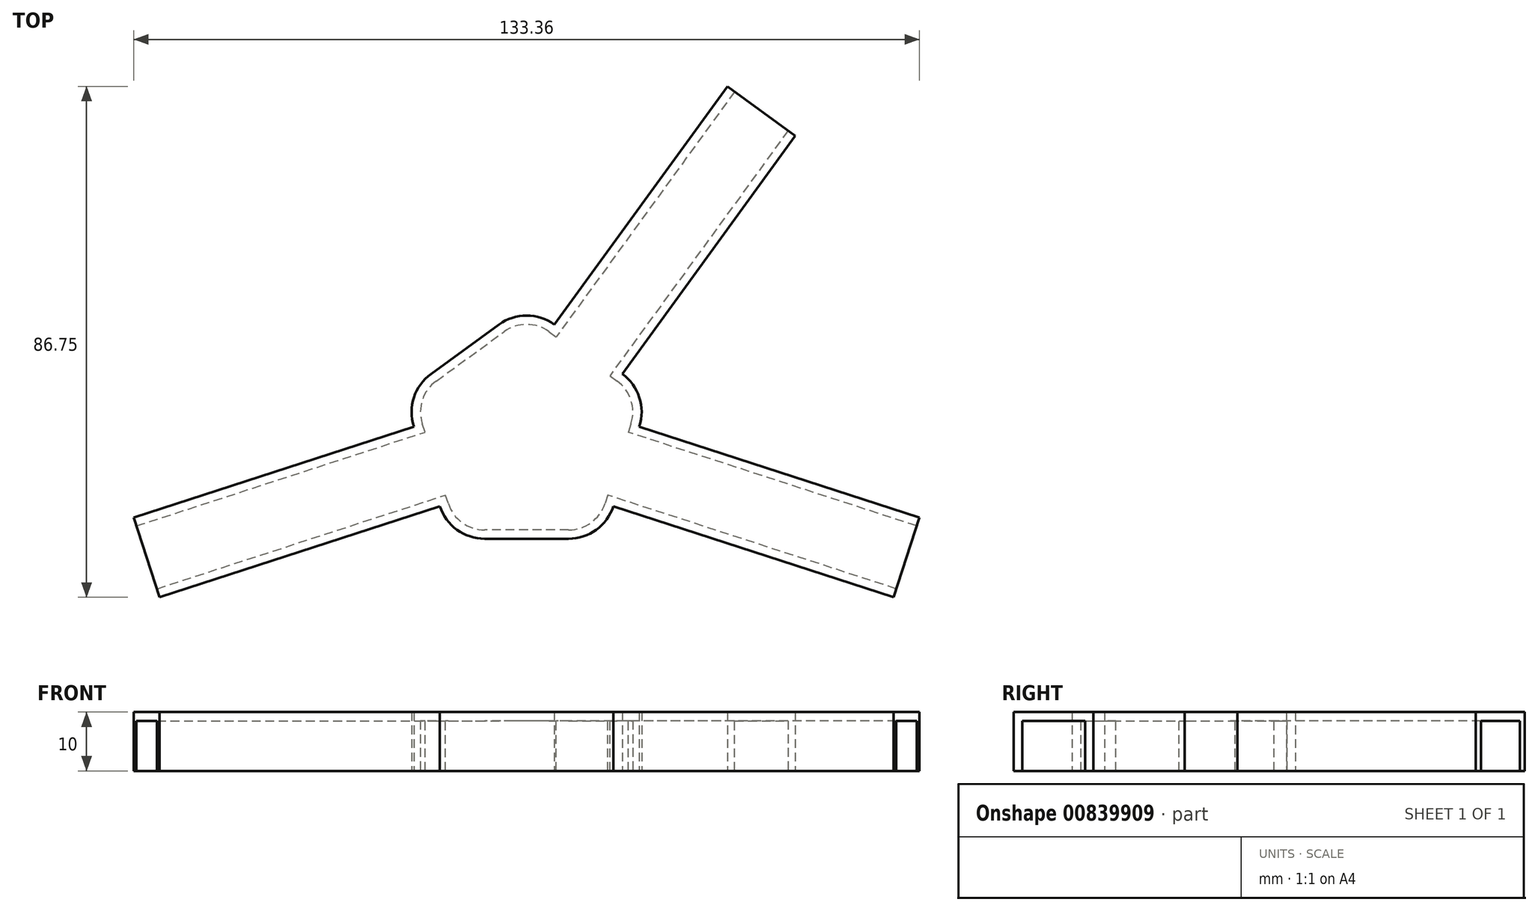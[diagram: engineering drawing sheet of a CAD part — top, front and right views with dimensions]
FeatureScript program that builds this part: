
annotation { "Feature Type Name" : "Feature", "Feature Type Description" : "" }
export const myFeature = defineFeature(function(context is Context, id is Id, definition is map)
    precondition{}
    {
        {
            var Q0;
            Q0=qCreatedBy(makeId("Top.planeOp"),FACE);
            var sketch = newSketch(context, id + "F0", { "sketchPlane" : qUnion([Q0])});
            skCircle(sketch, "E0.cCircle", {"center": v(0, 0) * mm, "radius": 22 * mm, "construction": true});
            skLineSegment(sketch, "E0.0", {"start": v(0, 22) * mm, "end": v(20.92, 6.8) * mm});
            skLineSegment(sketch, "E0.1", {"start": v(20.92, 6.8) * mm, "end": v(12.93, -17.8) * mm});
            skLineSegment(sketch, "E0.2", {"start": v(12.93, -17.8) * mm, "end": v(-12.93, -17.8) * mm});
            skLineSegment(sketch, "E0.3", {"start": v(-12.93, -17.8) * mm, "end": v(-20.92, 6.8) * mm});
            skLineSegment(sketch, "E0.4", {"start": v(-20.92, 6.8) * mm, "end": v(0, 22) * mm});
            skSolve(sketch);
        }
        {
            var Q0;
            Q0=makeQuery(id+"F0.imprint","IMPRINT",FACE,{"disambiguationData":[TD([[makeQuery(id+"F0.imprint","IMPRINT",EDGE,{"derivedFrom":sQuery(id+"F0.wireOp",EDGE,"E0.0")}),-1.0]])]});
            extrude(context, id + "F1", {"entities" : qUnion([Q0]), "depth" : 10 * mm, "offsetDistance" : 25 * mm});
        }
        {
            var Q0;
            Q0=makeQuery(id+"F1.opExtrude","SWEPT_EDGE",EDGE,{"disambiguationData":[OSD([sQuery(id+"F0.wireOp",EDGE,"E0.0"),sQuery(id+"F0.wireOp",EDGE,"E0.1")])]});
            var Q1;
            Q1=makeQuery(id+"F1.opExtrude","SWEPT_EDGE",EDGE,{"disambiguationData":[OSD([sQuery(id+"F0.wireOp",EDGE,"E0.0"),sQuery(id+"F0.wireOp",EDGE,"E0.4")])]});
            var Q2;
            Q2=makeQuery(id+"F1.opExtrude","SWEPT_EDGE",EDGE,{"disambiguationData":[OSD([sQuery(id+"F0.wireOp",EDGE,"E0.1"),sQuery(id+"F0.wireOp",EDGE,"E0.2")])]});
            var Q3;
            Q3=makeQuery(id+"F1.opExtrude","SWEPT_EDGE",EDGE,{"disambiguationData":[OSD([sQuery(id+"F0.wireOp",EDGE,"E0.2"),sQuery(id+"F0.wireOp",EDGE,"E0.3")])]});
            var Q4;
            Q4=makeQuery(id+"F1.opExtrude","SWEPT_EDGE",EDGE,{"disambiguationData":[OSD([sQuery(id+"F0.wireOp",EDGE,"E0.3"),sQuery(id+"F0.wireOp",EDGE,"E0.4")])]});
            fillet(context, id + "F2", {"entities" : qUnion([Q0, Q1, Q2, Q3, Q4]), "radius" : 8 * mm, "tangentPropagation" : true, "allowEdgeOverflow" : false});
        }
        {
            var Q0;
            Q0=makeQuery(id+"F1.opExtrude","CAP_FACE",FACE,{"disambiguationData":[OSD([sQuery(id+"F0.wireOp",EDGE,"E0.0"),sQuery(id+"F0.wireOp",EDGE,"E0.1"),sQuery(id+"F0.wireOp",EDGE,"E0.2"),sQuery(id+"F0.wireOp",EDGE,"E0.3"),sQuery(id+"F0.wireOp",EDGE,"E0.4")])],"isStart":true});
            shell(context, id + "F3", {"entities" : qUnion([Q0]), "thickness" : 1.5 * mm});
        }
        {
            var Q0;
            Q0=makeQuery(id+"F1.opExtrude","SWEPT_FACE",FACE,{"disambiguationData":[OSD([sQuery(id+"F0.wireOp",EDGE,"E0.1")])]});
            var sketch = newSketch(context, id + "F4", { "sketchPlane" : qUnion([Q0])});
            skLineSegment(sketch, "E1.bottom", {"start": v(-7.12, 10) * mm, "end": v(7.12, 10) * mm});
            skLineSegment(sketch, "E1.top", {"start": v(-7.12, 0) * mm, "end": v(7.12, 0) * mm});
            skLineSegment(sketch, "E1.left", {"start": v(-7.12, 10) * mm, "end": v(-7.12, 0) * mm});
            skLineSegment(sketch, "E1.right", {"start": v(7.12, 10) * mm, "end": v(7.12, 0) * mm});
            skPoint(sketch, "E1.middle", {"position": v(0, 5) * mm});
            skSolve(sketch);
        }
        {
            var Q0;
            Q0=makeQuery(id+"F4.imprint","IMPRINT",FACE,{"disambiguationData":[TD([[makeQuery(id+"F4.imprint","IMPRINT",EDGE,{"derivedFrom":sQuery(id+"F4.wireOp",EDGE,"E1.bottom")}),1.0]])]});
            extrude(context, id + "F5", {"entities" : qUnion([Q0]), "operationType" : NewBodyOperationType.ADD, "depth" : 50 * mm, "offsetDistance" : 25 * mm});
        }
        {
            var Q0;
            Q0=makeQuery(id+"F1.opExtrude","SWEPT_FACE",FACE,{"disambiguationData":[OSD([sQuery(id+"F0.wireOp",EDGE,"E0.3")])]});
            var sketch = newSketch(context, id + "F6", { "sketchPlane" : qUnion([Q0])});
            skLineSegment(sketch, "E2.bottom", {"start": v(-7.12, 10) * mm, "end": v(7.12, 10) * mm});
            skLineSegment(sketch, "E2.top", {"start": v(-7.12, 0) * mm, "end": v(7.12, 0) * mm});
            skLineSegment(sketch, "E2.left", {"start": v(-7.12, 10) * mm, "end": v(-7.12, 0) * mm});
            skLineSegment(sketch, "E2.right", {"start": v(7.12, 10) * mm, "end": v(7.12, 0) * mm});
            skPoint(sketch, "E2.middle", {"position": v(0, 5) * mm});
            skSolve(sketch);
        }
        {
            var Q0;
            Q0=makeQuery(id+"F1.opExtrude","SWEPT_FACE",FACE,{"disambiguationData":[OSD([sQuery(id+"F0.wireOp",EDGE,"E0.0")])]});
            var sketch = newSketch(context, id + "F7", { "sketchPlane" : qUnion([Q0])});
            skLineSegment(sketch, "E3.bottom", {"start": v(-7.12, 10) * mm, "end": v(7.12, 10) * mm});
            skLineSegment(sketch, "E3.top", {"start": v(-7.12, 0) * mm, "end": v(7.12, 0) * mm});
            skLineSegment(sketch, "E3.left", {"start": v(-7.12, 10) * mm, "end": v(-7.12, 0) * mm});
            skLineSegment(sketch, "E3.right", {"start": v(7.12, 10) * mm, "end": v(7.12, 0) * mm});
            skPoint(sketch, "E3.middle", {"position": v(0, 5) * mm});
            skSolve(sketch);
        }
        {
            var Q0;
            Q0=makeQuery(id+"F7.imprint","IMPRINT",FACE,{"disambiguationData":[TD([[makeQuery(id+"F7.imprint","IMPRINT",EDGE,{"derivedFrom":sQuery(id+"F7.wireOp",EDGE,"E3.bottom")}),1.0]])]});
            extrude(context, id + "F8", {"entities" : qUnion([Q0]), "operationType" : NewBodyOperationType.ADD, "depth" : 50 * mm, "offsetDistance" : 25 * mm});
        }
        {
            var Q0;
            Q0=makeQuery(id+"F6.imprint","IMPRINT",FACE,{"disambiguationData":[TD([[makeQuery(id+"F6.imprint","IMPRINT",EDGE,{"derivedFrom":sQuery(id+"F6.wireOp",EDGE,"E2.bottom")}),1.0]])]});
            extrude(context, id + "F9", {"entities" : qUnion([Q0]), "operationType" : NewBodyOperationType.ADD, "depth" : 50 * mm, "offsetDistance" : 25 * mm});
        }
        {
            var Q0;
            Q0=makeQuery(id+"F8.opExtrude","CAP_FACE",FACE,{"disambiguationData":[OSD([sQuery(id+"F7.wireOp",EDGE,"E3.bottom"),sQuery(id+"F7.wireOp",EDGE,"E3.top"),sQuery(id+"F7.wireOp",EDGE,"E3.left"),sQuery(id+"F7.wireOp",EDGE,"E3.right")])],"isStart":false});
            var Q1;
            Q1=makeQuery(id+"F3.opShell","OFFSET_FACE",FACE,{"disambiguationData":[OSD([sQuery(id+"F0.wireOp",EDGE,"E0.0")])]});
            var Q2;
            Q2=makeQuery(id+"F9.opExtrude","CAP_FACE",FACE,{"disambiguationData":[OSD([sQuery(id+"F6.wireOp",EDGE,"E2.bottom"),sQuery(id+"F6.wireOp",EDGE,"E2.top"),sQuery(id+"F6.wireOp",EDGE,"E2.left"),sQuery(id+"F6.wireOp",EDGE,"E2.right")])],"isStart":false});
            var Q3;
            Q3=makeQuery(id+"F3.opShell","OFFSET_FACE",FACE,{"disambiguationData":[OSD([sQuery(id+"F0.wireOp",EDGE,"E0.3")])]});
            var Q4;
            Q4=makeQuery(id+"F5.opExtrude","CAP_FACE",FACE,{"disambiguationData":[OSD([sQuery(id+"F4.wireOp",EDGE,"E1.bottom"),sQuery(id+"F4.wireOp",EDGE,"E1.top"),sQuery(id+"F4.wireOp",EDGE,"E1.left"),sQuery(id+"F4.wireOp",EDGE,"E1.right")])],"isStart":false});
            var Q5;
            Q5=makeQuery(id+"F3.opShell","OFFSET_FACE",FACE,{"disambiguationData":[OSD([sQuery(id+"F0.wireOp",EDGE,"E0.1")])]});
            var Q6;
            Q6=makeQuery(id+"F9.boolean.opBoolean","MERGE",FACE,{"derivedFrom":[makeQuery(id+"F8.boolean.opBoolean","MERGE",FACE,{"derivedFrom":[makeQuery(id+"F5.boolean.opBoolean","MERGE",FACE,{"derivedFrom":[makeQuery(id+"F1.opExtrude","CAP_FACE",FACE,{"disambiguationData":[OSD([sQuery(id+"F0.wireOp",EDGE,"E0.0"),sQuery(id+"F0.wireOp",EDGE,"E0.1"),sQuery(id+"F0.wireOp",EDGE,"E0.2"),sQuery(id+"F0.wireOp",EDGE,"E0.3"),sQuery(id+"F0.wireOp",EDGE,"E0.4")])],"isStart":true}),makeQuery(id+"F5.opExtrude","SWEPT_FACE",FACE,{"disambiguationData":[OSD([sQuery(id+"F4.wireOp",EDGE,"E1.top")])]})]}),makeQuery(id+"F8.opExtrude","SWEPT_FACE",FACE,{"disambiguationData":[OSD([sQuery(id+"F7.wireOp",EDGE,"E3.top")])]})]}),makeQuery(id+"F9.opExtrude","SWEPT_FACE",FACE,{"disambiguationData":[OSD([sQuery(id+"F6.wireOp",EDGE,"E2.top")])]})]});
            shell(context, id + "F10", {"entities" : qUnion([Q0, Q1, Q2, Q3, Q4, Q5, Q6]), "thickness" : 1.5 * mm});
        }
    });
